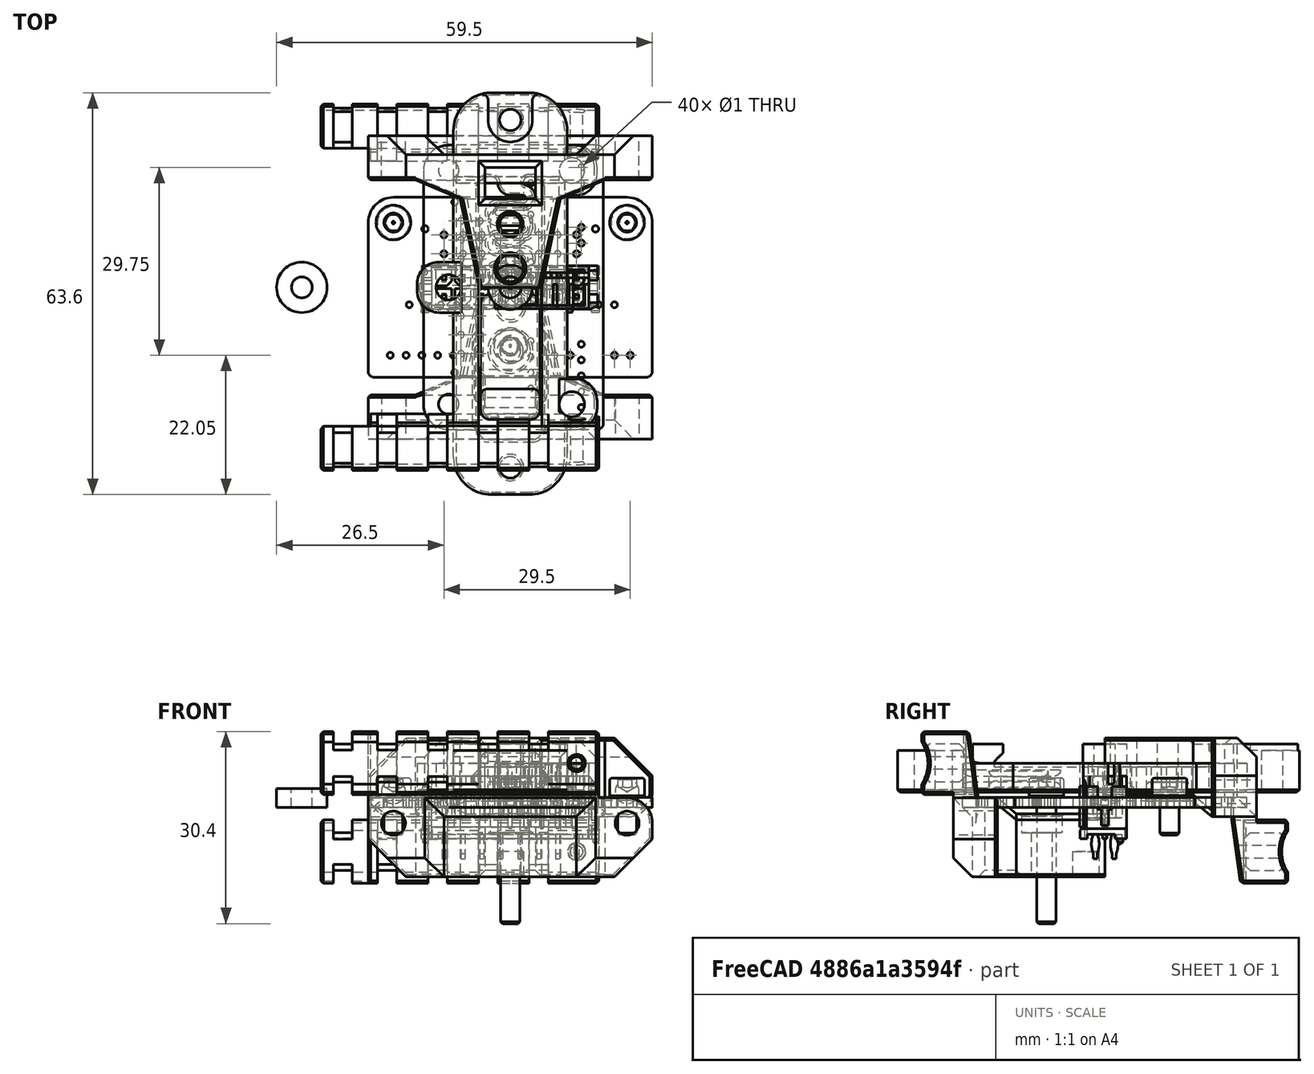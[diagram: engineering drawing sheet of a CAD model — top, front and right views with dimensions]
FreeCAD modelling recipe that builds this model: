
FCSTD DOCUMENT  (FreeCAD 0.19R24366 (Git))
Label: pcb-mounter
License: Other
LicenseURL: GPL3
objects: Part::Chamfer×20, Part::Feature×19, Part::Box×17, Part::MultiFuse×11, App::Part×10, Part::Cut×9, Part::Cylinder×7, Part::FeaturePython×4, Part::Fillet×2
note: 89 computed .brp shape members not serialized (recipe doc carries the construction recipe); baked Part::Feature solids carry a one-line shape summary decoded from their .brp

FEATURE [Part::Feature] Fusion001010
  Placement = pos=(-16,0,0) rot=(0,0,1;0rad)
  shape: bbox 3 x 9 x 10.5 mm, 12 faces, 2 solids (baked)
FEATURE [Part::Feature] Fusion001011
  Placement = pos=(-24,0,0) rot=(0,0,1;0rad)
  shape: bbox 3 x 9 x 10.5 mm, 12 faces, 2 solids (baked)
FEATURE [Part::Feature] Fusion001012
  Placement = pos=(-8,0,0) rot=(0,0,1;0rad)
  shape: bbox 3 x 9 x 10.5 mm, 12 faces, 2 solids (baked)
FEATURE [Part::Box] Box017  label="Cube017"
  AttacherType = Attacher::AttachEngine3D
  Height = 29
  Length = 8
  Placement = pos=(-4,14,-16) rot=(0,0,1;0rad)
  Width = 5
FEATURE [Part::Cylinder] Cylinder004
  Angle = 360
  AttacherType = Attacher::AttachEngine3D
  Height = 23
  Placement = pos=(10.5,13,-7) rot=(-1,0,0;1.5708rad)
  Radius = 1
FEATURE [Part::Box] Box020  label="Cube020"
  AttacherType = Attacher::AttachEngine3D
  Height = 2.5
  Length = 3
  Placement = pos=(3,22,-12.5) rot=(0,0,1;0rad)
  Width = 9
FEATURE [Part::Box] Box021  label="Cube021"
  AttacherType = Attacher::AttachEngine3D
  Height = 14
  Length = 27
  Placement = pos=(-13.5,26,-3) rot=(0,0,1;0rad)
  Width = 7
FEATURE [Part::Cylinder] Cylinder005
  Angle = 360
  AttacherType = Attacher::AttachEngine3D
  Height = 10
  Placement = pos=(18.5,29,5.5) rot=(-1,0,0;1.5708rad)
  Radius = 1.9
FEATURE [Part::Feature] Fusion001016
  Placement = pos=(-31,0,0) rot=(0,0,1;0rad)
  shape: bbox 3 x 9 x 10.5 mm, 12 faces, 2 solids (baked)
FEATURE [Part::Feature] Cut002003002014
  shape: bbox 15.84 x 14 x 11 mm, 11 faces (baked)
FEATURE [Part::Cylinder] Cylinder006
  Angle = 360
  AttacherType = Attacher::AttachEngine3D
  Height = 55
  Placement = pos=(19.5,34,-7) rot=(0.57735,0.57735,-0.57735;4.18879rad)
  Radius = 6
FEATURE [Part::Box] Box023  label="Cube023"
  AttacherType = Attacher::AttachEngine3D
  Height = 10
  Length = 58
  Placement = pos=(-33,26,8) rot=(0,0,1;0rad)
  Width = 10
FEATURE [Part::Chamfer] Chamfer001002006005039
  Base = -> Box023
  Edges = 1 edges r=3: [Edge9]
FEATURE [Part::Box] Box024  label="Cube024"
  AttacherType = Attacher::AttachEngine3D
  Height = 2
  Length = 3
  Placement = pos=(3,22,-4) rot=(0,0,1;0rad)
  Width = 9
FEATURE [Part::MultiFuse] Fusion001013
  Shapes = -> [Box024,Box020]
FEATURE [Part::MultiFuse] Fusion001014
  Shapes = -> [Fusion001016,Fusion001011,Fusion001010,Fusion001012,Fusion001013]
FEATURE [Part::Chamfer] Chamfer001002006005041
  Base = -> Box021
  Edges = 3 edges r=3: [Edge1,Edge5,Edge9]
  Placement = pos=(0,0,1.5) rot=(0,0,1;0rad)
FEATURE [Part::MultiFuse] Fusion001019
  Placement = pos=(0,-5,0) rot=(0,0,1;0rad)
  Shapes = -> [Chamfer001002006005041,Chamfer001002006005039]
FEATURE [Part::Cylinder] Cylinder007
  Angle = 360
  AttacherType = Attacher::AttachEngine3D
  Height = 10
  Placement = pos=(-18.5,29,5.5) rot=(-1,0,0;1.5708rad)
  Radius = 1.9
FEATURE [Part::MultiFuse] Fusion001017
  Placement = pos=(0,-14,-3) rot=(0,0,1;0rad)
  Shapes = -> [Cylinder007,Cylinder005]
FEATURE [Part::Box] Box026  label="Cube026"
  AttacherType = Attacher::AttachEngine3D
  Height = 12.5
  Length = 30
  Placement = pos=(-15,14,-1.5) rot=(0,0,1;0rad)
  Width = 4
FEATURE [Part::Feature] Part__Feature112001168  label="SOLID004"
  shape: bbox 12.4 x 5.75 x 10.4 mm, 141 faces (baked)
FEATURE [App::Part] JST_XH_B04B_XH_A_1x04_P2_50mm_Vertical  label="JST_XH_B04B-XH-A_1x04_P2.50mm_Vertical"
  Group = -> [Part__Feature112001168]
  Origin = -> Origin216
  Placement = pos=(-8.5,-2.75,1.65) rot=(0,0,1;3.14159rad)
FEATURE [Part::Feature] Part__Feature112001167  label="SOLID003"
  shape: bbox 9.9 x 5.75 x 10.4 mm, 117 faces (baked)
FEATURE [Part::FeaturePython] Screw003  label="M3x20-Screw025"  # Fasteners workbench fastener (typed FeaturePython)
  Placement = pos=(0,-9.25,1.6) rot=(0,0,1;0rad)
  baseObject = -> Part__Feature112001171 [Edge92]
  diameter = 4
  invert = false
  leftHanded = false
  length = 7
  lengthCustom = 20
  matchOuter = true
  offset = 0
  thread = false
  type = 34
FEATURE [Part::Feature] Part__Feature112001170  label="SOLID006"
  shape: bbox 2 x 1.25 x 1.25 mm, 28 faces (baked)
FEATURE [App::Part] C_0805_2012Metric
  Group = -> [Part__Feature112001170]
  Origin = -> Origin218
  Placement = pos=(-20.5,-3.225,1.65) rot=(0,0,1;1.5708rad)
FEATURE [Part::Feature] Part__Feature112001169  label="SOLID005"
  shape: bbox 14.9 x 5.75 x 10.4 mm, 165 faces (baked)
FEATURE [App::Part] JST_XH_B05B_XH_A_1x05_P2_50mm_Vertical  label="JST_XH_B05B-XH-A_1x05_P2.50mm_Vertical"
  Group = -> [Part__Feature112001169]
  Origin = -> Origin217
  Placement = pos=(-9,-10.75,1.65) rot=(0,0,1;3.14159rad)
FEATURE [App::Part] JST_XH_B03B_XH_A_1x03_P2_50mm_Vertical001  label="JST_XH_B03B-XH-A_1x03_P2.50mm_Vertical001"
  Group = -> [Part__Feature112001167]
  Origin = -> Origin215
  Placement = pos=(4,-2.75,1.65) rot=(0,0,1;3.14159rad)
FEATURE [Part::Feature] Part__Feature112001166  label="SOLID002"
  shape: bbox 7.4 x 5.75 x 10.4 mm, 89 faces (baked)
FEATURE [App::Part] JST_XH_B02B_XH_A_1x02_P2_50mm_Vertical001  label="JST_XH_B02B-XH-A_1x02_P2.50mm_Vertical001"
  Group = -> [Part__Feature112001166]
  Origin = -> Origin214
  Placement = pos=(9.5,-10.75,1.65) rot=(0,0,1;3.14159rad)
FEATURE [Part::Feature] Part__Feature112001171  label="COMPOUND002"
  shape: bbox 45 x 28.5 x 1.6 mm, 50 faces (baked)
FEATURE [Part::Feature] Part__Feature112001163  label="SOLID"
  shape: bbox 9.9 x 5.75 x 10.4 mm, 117 faces (baked)
FEATURE [Part::Feature] Part__Feature112001165  label="SOLID001"
  shape: bbox 7.4 x 5.75 x 10.4 mm, 89 faces (baked)
FEATURE [App::Part] JST_XH_B02B_XH_A_1x02_P2_50mm_Vertical  label="JST_XH_B02B-XH-A_1x02_P2.50mm_Vertical"
  Group = -> [Part__Feature112001165]
  Origin = -> Origin213
  Placement = pos=(19,-10.75,1.65) rot=(0,0,1;3.14159rad)
FEATURE [Part::Feature] Part__Feature112001164  label="COMPOUND"
  shape: bbox 28.15 x 8.8 x 13.09 mm, 388 faces (baked)
FEATURE [App::Part] COMPOUND  label="COMPOUND001"
  Group = -> [Part__Feature112001164]
  Origin = -> Origin211
FEATURE [App::Part] microfit_16  label="microfit-16"
  Group = -> [COMPOUND]
  Origin = -> Origin212
  Placement = pos=(-6e-06,6.81,6.65) rot=(0,0,1;0rad)
FEATURE [App::Part] JST_XH_B03B_XH_A_1x03_P2_50mm_Vertical  label="JST_XH_B03B-XH-A_1x03_P2.50mm_Vertical"
  Group = -> [Part__Feature112001163]
  Origin = -> Origin210
  Placement = pos=(16.5,-2.75,1.65) rot=(0,0,1;3.14159rad)
FEATURE [Part::FeaturePython] Screw001  label="M3x6-Screw001"  # Fasteners workbench fastener (typed FeaturePython)
  Placement = pos=(18.5,10.25,1.6) rot=(0,0,1;0rad)
  baseObject = -> Part__Feature112001171 [Edge78]
  diameter = 4
  invert = false
  leftHanded = false
  length = 1
  lengthCustom = 6
  matchOuter = true
  offset = 0
  thread = false
  type = 34
FEATURE [Part::FeaturePython] Screw002  label="M3x6-Screw"  # Fasteners workbench fastener (typed FeaturePython)
  Placement = pos=(-18.5,10.25,1.6) rot=(0,0,1;0rad)
  baseObject = -> Part__Feature112001171 [Edge81]
  diameter = 4
  invert = false
  leftHanded = false
  length = 1
  lengthCustom = 6
  matchOuter = true
  offset = 0
  thread = false
  type = 34
FEATURE [App::Part] Open_CASCADE_STEP_translator_6_9_1  label="PCB-rev1"
  Group = -> [JST_XH_B03B_XH_A_1x03_P2_50mm_Vertical,microfit_16,JST_XH_B02B_XH_A_1x02_P2_50mm_Vertical,JST_XH_B02B_XH_A_1x02_P2_50mm_Vertical001,JST_XH_B03B_XH_A_1x03_P2_50mm_Vertical001,JST_XH_B04B_XH_A_1x04_P2_50mm_Vertical,JST_XH_B05B_XH_A_1x05_P2_50mm_Vertical,C_0805_2012Metric,Part__Feature112001171,Screw002,Screw001,Screw003]
  Origin = -> Origin219
  Placement = pos=(0,24.05,12.75) rot=(1,0,0;4.71239rad)
FEATURE [Part::Box] Box027  label="Cube027"
  AttacherType = Attacher::AttachEngine3D
  Height = 10
  Length = 44
  Placement = pos=(-30,22,-12) rot=(0,0,1;0rad)
  Width = 7
FEATURE [Part::Box] Box028  label="Cube028"
  AttacherType = Attacher::AttachEngine3D
  Height = 12.5
  Length = 45
  Placement = pos=(-22.5,17,-1.5) rot=(0,0,1;0rad)
  Width = 7
FEATURE [Part::Fillet] Fillet002
  Base = -> Box028
  Edges = 2 edges r=4: [Edge4,Edge8]
FEATURE [Part::Chamfer] Chamfer001002006005046
  Base = -> Fillet002
  Edges = 2 edges r=6: [Edge4,Edge13]
FEATURE [Part::Chamfer] Chamfer001002006005047
  Base = -> Cut002003002014
  Edges = 4 edges r=0.4: [Edge7,Edge10,Edge14,Edge15]
FEATURE [Part::Chamfer] Chamfer001002006005049
  Base = -> Box026
  Edges = 1 edges: [Edge5 r1=3 r2=7.08]
FEATURE [Part::Feature] Fusion001014001
  Placement = pos=(0,-9,0) rot=(0,0,1;0rad)
  shape: bbox 34 x 9 x 10.5 mm, 60 faces, 10 solids (baked)
FEATURE [Part::MultiFuse] Fusion001014002
  Shapes = -> [Fusion001014001,Fusion001014]
FEATURE [Part::Box] Box029  label="Cube029"
  AttacherType = Attacher::AttachEngine3D
  Height = 15.5
  Length = 36.5
  Placement = pos=(-22.5,20,-12) rot=(0,0,1;0rad)
  Width = 4
FEATURE [Part::Cut] Cut002003002017
  Base = -> Box027
  Tool = -> Cylinder006
FEATURE [Part::Chamfer] Chamfer001002006005059
  Base = -> Cut002003002017
  Edges = 13 edges r=0.4: [Edge1,Edge2,Edge3,Edge4,Edge5,Edge6,Edge7,Edge8,Edge10,Edge12,Edge14,Edge15,Edge16]
FEATURE [Part::Box] Box030  label="Cube030"
  AttacherType = Attacher::AttachEngine3D
  Height = 10
  Length = 3
  Placement = pos=(-21,10.5,-13.5) rot=(0,0,1;0rad)
  Width = 10
FEATURE [Part::Box] Box031  label="Cube031"
  AttacherType = Attacher::AttachEngine3D
  Height = 10
  Length = 3
  Placement = pos=(-13,10.5,-13.5) rot=(0,0,1;0rad)
  Width = 10
FEATURE [Part::Box] Box032  label="Cube032"
  AttacherType = Attacher::AttachEngine3D
  Height = 10
  Length = 3
  Placement = pos=(-5,10.5,-13.5) rot=(0,0,1;0rad)
  Width = 10
FEATURE [Part::Box] Box033  label="Cube033"
  AttacherType = Attacher::AttachEngine3D
  Height = 10
  Length = 3
  Placement = pos=(3,10.5,-13.5) rot=(0,0,1;0rad)
  Width = 10
FEATURE [Part::MultiFuse] Fusion001014004
  Placement = pos=(0,1.5,0) rot=(0,0,1;0rad)
  Shapes = -> [Box033,Box030,Box031,Box032]
FEATURE [Part::Chamfer] Chamfer001002006005063
  Base = -> Chamfer001002006005046
  Edges = 8 edges r=0.4: [Edge1,Edge5,Edge6,Edge7,Edge8,Edge9,Edge10,Edge11]
FEATURE [Part::Box] Box034  label="Cube034"
  AttacherType = Attacher::AttachEngine3D
  Height = 1
  Length = 19
  Placement = pos=(-10,-3,0) rot=(0,0,1;0rad)
  Width = 22
FEATURE [Part::Cut] Cut002003002021
  Base = -> Chamfer001002006005047
  Tool = -> Box034
FEATURE [Part::Chamfer] Chamfer001002006005064
  Base = -> Cut002003002021
  Edges = 2 edges r=1: [Edge7,Edge9]
FEATURE [Part::Chamfer] Chamfer001002006005050
  Base = -> Chamfer001002006005049
  Edges = 1 edges: [Edge15 r1=7.08 r2=3]
FEATURE [Part::Chamfer] Chamfer001002006005051
  Base = -> Chamfer001002006005050
  Edges = 1 edges: [Edge14 r1=2.5 r2=3]
FEATURE [Part::Chamfer] Chamfer001002006005065
  Base = -> Chamfer001002006005051
  Edges = 1 edges: [Edge11 r1=0.17 r2=0.4]
FEATURE [Part::Chamfer] Chamfer001002006005066
  Base = -> Chamfer001002006005065
  Edges = 1 edges: [Edge10 r1=0.17 r2=0.4]
FEATURE [Part::Chamfer] Chamfer001002006005067
  Base = -> Chamfer001002006005066
  Edges = 1 edges: [Edge18 r1=0.95 r2=0.5]
FEATURE [Part::Chamfer] Chamfer001002006005068
  Base = -> Chamfer001002006005067
  Edges = 1 edges: [Edge17 r1=0.5 r2=0.95]
FEATURE [Part::Chamfer] Chamfer001002006005069
  Base = -> Chamfer001002006005064
  Edges = 1 edges r=0.4: [Edge12]
FEATURE [Part::Chamfer] Chamfer001002006005070
  Base = -> Box029
  Edges = 1 edges: [Edge9 r1=10.5 r2=1.5]
FEATURE [Part::Chamfer] Chamfer001002006005071
  Base = -> Chamfer001002006005070
  Edges = 6 edges r=0.4: [Edge1,Edge2,Edge3,Edge9,Edge10,Edge13]
FEATURE [Part::MultiFuse] Fusion001014005
  Shapes = -> [Chamfer001002006005059,Chamfer001002006005071]
FEATURE [Part::Cut] Cut002003002022
  Base = -> Fusion001014005
  Tool = -> Fusion001014002
FEATURE [Part::Cut] Cut002003002023
  Base = -> Cut002003002022
  Tool = -> Fusion001014004
FEATURE [Part::MultiFuse] Fusion001014006
  Shapes = -> [Chamfer001002006005069,Chamfer001002006005068,Chamfer001002006005063,Cut002003002023]
FEATURE [Part::Cut] Cut002003002024
  Base = -> Fusion001014006
  Tool = -> Fusion001019
FEATURE [Part::Cut] Cut002003002025
  Base = -> Cut002003002024
  Tool = -> Fusion001017
FEATURE [Part::Cut] Cut002003002026
  Base = -> Cut002003002025
  Refine = true
  Tool = -> Cylinder004
FEATURE [Part::Cut] Cut002003002027
  Base = -> Cut002003002026
  Tool = -> Box017
FEATURE [Part::Chamfer] Chamfer001002006005072
  Base = -> Cut002003002027
  Edges = 24 edges r=1: [Edge88,Edge89,Edge96,Edge97,Edge98,Edge99,Edge106,Edge107,Edge114,Edge115,Edge123,Edge125,Edge199,Edge201,Edge269,Edge270,Edge275,Edge276,Edge289,Edge291,Edge321,Edge322,Edge323,Edge324]
FEATURE [Part::Chamfer] Chamfer001002006005073
  Base = -> Chamfer001002006005072
  Edges = 2 edges r=0.4: [Edge89,Edge124]
FEATURE [Part::Feature] Chamfer001002006005073001
  Placement = pos=(0,0,0) rot=(1,0,0;3.14159rad)
  shape: bbox 52.5 x 29 x 23 mm, 192 faces (baked)
FEATURE [Part::Feature] Tube001
  shape: bbox 7 x 7 x 10 mm, 4 faces (baked)
FEATURE [Part::Feature] Part__Feature822001001  label="RS-25 PSU Bracket003"
  Placement = pos=(0,0,4.6) rot=(0,0,1;0rad)
  shape: bbox 18 x 63.6 x 7.6 mm, 163 faces (baked)
FEATURE [Part::Feature] Part__Feature822001002  label="COMPOUND003"
  Placement = pos=(0.5,-1e-16,0) rot=(0,0,1;1.5708rad)
  shape: bbox 28.5 x 45 x 1.6 mm, 50 faces (baked)
FEATURE [Part::Cylinder] Cylinder
  Angle = 360
  AttacherType = Attacher::AttachEngine3D
  Height = 10
  Placement = pos=(-9.75,18.5,0) rot=(0,0,1;0rad)
  Radius = 2
FEATURE [Part::Cylinder] Cylinder008
  Angle = 360
  AttacherType = Attacher::AttachEngine3D
  Height = 10
  Placement = pos=(-9.75,-18.5,0) rot=(0,0,1;0rad)
  Radius = 2
FEATURE [Part::Cylinder] Cylinder009
  Angle = 360
  AttacherType = Attacher::AttachEngine3D
  Height = 10
  Placement = pos=(9.75,0,0) rot=(0,0,1;0rad)
  Radius = 2
FEATURE [Part::MultiFuse] Fusion
  Placement = pos=(0,0,-3) rot=(0,0,1;0rad)
  Shapes = -> [Cylinder,Cylinder008,Cylinder009]
FEATURE [Part::Box] Box  label="Cube"
  AttacherType = Attacher::AttachEngine3D
  Height = 4.6
  Length = 6
  Placement = pos=(-13.75,14.5,0) rot=(0,0,1;0rad)
  Width = 8
FEATURE [Part::Box] Box035  label="Cube035"
  AttacherType = Attacher::AttachEngine3D
  Height = 4.6
  Length = 7
  Placement = pos=(7.75,-4,0) rot=(0,0,1;0rad)
  Width = 8
FEATURE [Part::Box] Box036  label="Cube036"
  AttacherType = Attacher::AttachEngine3D
  Height = 4.6
  Length = 6
  Placement = pos=(-13.75,-22.5,0) rot=(0,0,1;0rad)
  Width = 8
FEATURE [Part::MultiFuse] Fusion001014007
  Shapes = -> [Box,Box035,Box036]
FEATURE [Part::Fillet] Fillet
  Base = -> Fusion001014007
  Edges = 6 edges r=3.5: [Edge1,Edge3,Edge17,Edge19,Edge25,Edge27]
FEATURE [Part::Chamfer] Chamfer
  Base = -> Fillet
  Edges = 15 edges r=0.4: [Edge1,Edge5,Edge6,Edge8,Edge9,Edge19,Edge23,Edge25,Edge26,Edge27,Edge37,Edge41,Edge42,Edge44,Edge45]
FEATURE [Part::MultiFuse] Fusion001014008
  Shapes = -> [Chamfer,Part__Feature822001001]
FEATURE [Part::Cut] Cut
  Base = -> Fusion001014008
  Placement = pos=(-9e-16,0,7) rot=(0,1,0;3.14159rad)
  Refine = true
  Tool = -> Fusion
FEATURE [Part::FeaturePython] Tube  # WARN: FeaturePython — macro-defined, semantics opaque (R4)
  AttacherType = Attacher::AttachEngine3D
  Height = 3
  InnerRadius = 1.65
  OuterRadius = 4
  Placement = pos=(-33,0,0) rot=(0,0,1;0rad)
